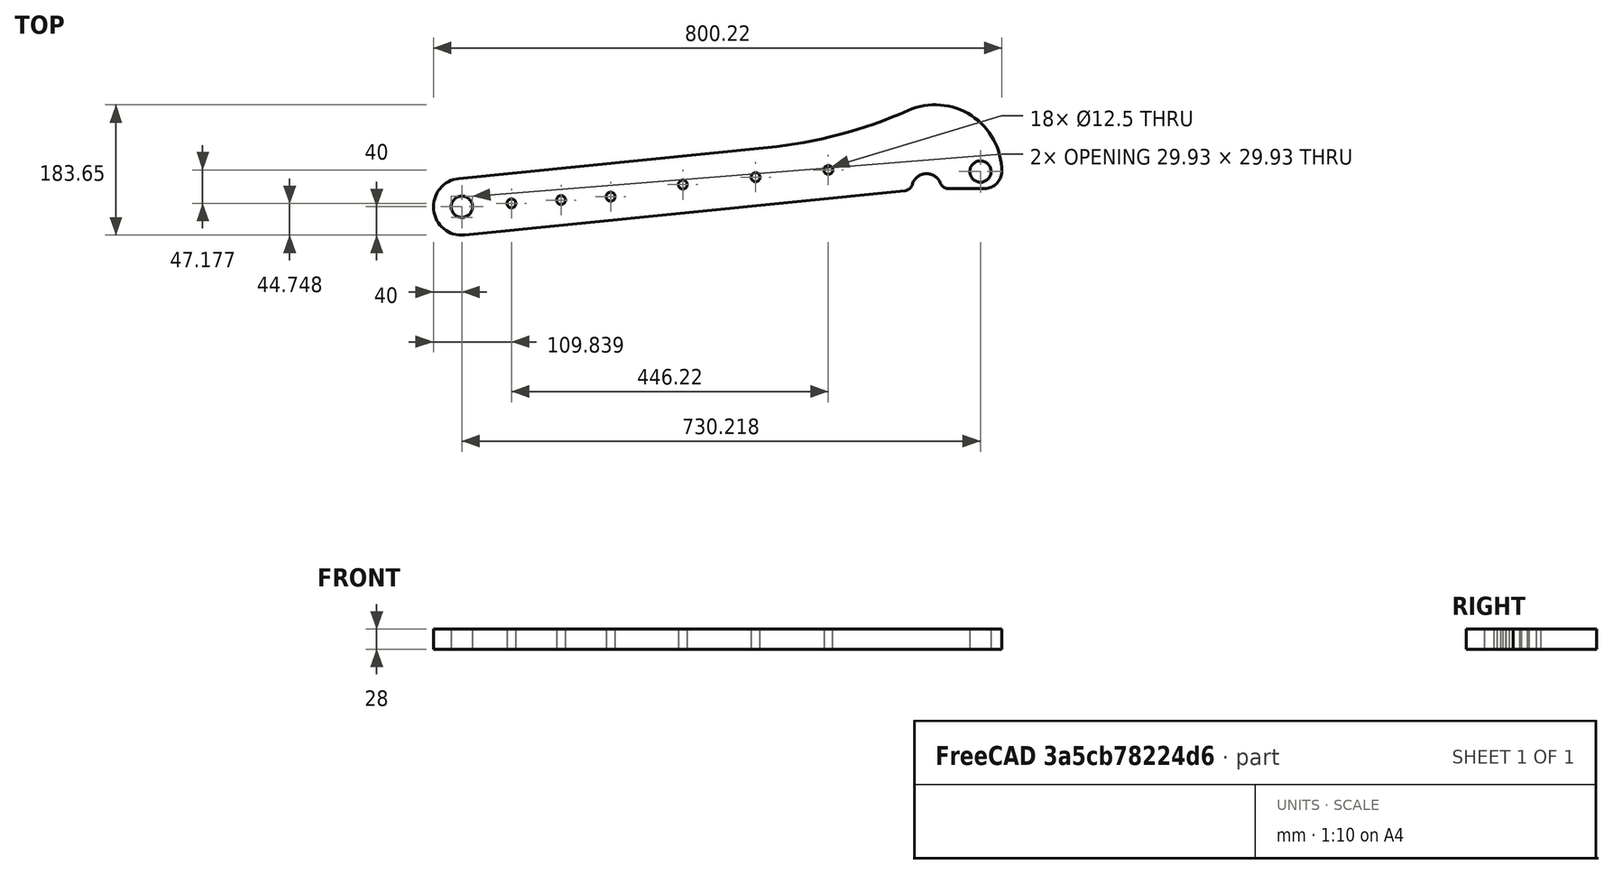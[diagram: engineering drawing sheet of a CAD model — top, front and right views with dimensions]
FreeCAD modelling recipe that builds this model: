
FCSTD DOCUMENT  (FreeCAD 0.19R24267 +99 (Git))
Label: V2 Stack pivot arm FEA_CLEARED
License: All rights reserved
LicenseURL: http://en.wikipedia.org/wiki/All_rights_reserved
objects: PartDesign::Pad×3, Fem::ConstraintForce×2, Sketcher::SketchObject×1, Fem::FemSolverObjectPython×1, App::MaterialObjectPython×1, Fem::FeaturePython×1, Fem::FemMeshObjectPython×1, Fem::ConstraintFixed×1, Fem::FemAnalysis×1, PartDesign::Body×1
note: 8 computed .brp shape members not serialized (recipe doc carries the construction recipe); baked Part::Feature solids carry a one-line shape summary decoded from their .brp

FEATURE [Sketcher::SketchObject] Sketch
  FullyConstrained = true
  MapMode = 5
  Support = -> [XY_Plane]
  sketch-geometry (36):
    g0: LineSegment StartX=730.218 StartY=49.6455 StartZ=0 EndX=730.218 EndY=0 EndZ=0
    g1: LineSegment StartX=730.218 StartY=25.6455 StartZ=0 EndX=685.168 EndY=25.6455 EndZ=0
    g2: Circle CenterX=730.218 CenterY=0 CenterZ=0 NormalX=0 NormalY=0 NormalZ=1 AngleXU=0 Radius=15
    g3: ArcOfCircle CenterX=0 CenterY=0 CenterZ=0 NormalX=0 NormalY=0 NormalZ=1 AngleXU=0 Radius=40 StartAngle=1.67108 EndAngle=4.81267
    g4: LineSegment StartX=4.00452 StartY=-39.799 StartZ=0 EndX=623.841 EndY=22.5679 EndZ=0
    g5: LineSegment StartX=730.218 StartY=25.6455 StartZ=0 EndX=736.218 EndY=25.6455 EndZ=0
    g6: ArcOfCircle CenterX=736.218 CenterY=49.6455 CenterZ=0 NormalX=0 NormalY=0 NormalZ=1 AngleXU=0 Radius=24 StartAngle=4.71239 EndAngle=6.28319
    g7: LineSegment StartX=430.857 StartY=83.5541 StartZ=0 EndX=-4.00452 EndY=39.799 EndZ=0
    g8: LineSegment StartX=0 StartY=0 StartZ=0 EndX=730.218 EndY=49.6455 EndZ=0
    g9: LineSegment StartX=0 StartY=0 StartZ=0 EndX=516.059 EndY=51.9251 EndZ=0
    g10: Circle CenterX=311.094 CenterY=31.3018 CenterZ=0 NormalX=0 NormalY=0 NormalZ=1 AngleXU=0 Radius=6.25
    g11: Circle CenterX=413.577 CenterY=41.6134 CenterZ=0 NormalX=0 NormalY=0 NormalZ=1 AngleXU=0 Radius=6.25
    g12: GeomPoint X=730.218 Y=24 Z=0
    g13: LineSegment StartX=0 StartY=0 StartZ=0 EndX=-1.01746 EndY=14.9655 EndZ=0
    g14: LineSegment StartX=0 StartY=0 StartZ=0 EndX=1.01746 EndY=-14.9655 EndZ=0
    g15: ArcOfCircle CenterX=0 CenterY=0 CenterZ=0 NormalX=0 NormalY=0 NormalZ=1 AngleXU=0 Radius=15 StartAngle=1.63868 EndAngle=4.78027
    g16: ArcOfCircle CenterX=0 CenterY=0 CenterZ=0 NormalX=0 NormalY=0 NormalZ=1 AngleXU=0 Radius=15 StartAngle=4.78027 EndAngle=7.92186
    g17: LineSegment StartX=730.218 StartY=49.6455 StartZ=0 EndX=729.201 EndY=64.611 EndZ=0
    g18: LineSegment StartX=730.218 StartY=49.6455 StartZ=0 EndX=731.236 EndY=34.68 EndZ=0
    g19: ArcOfCircle CenterX=730.218 CenterY=49.6455 CenterZ=0 NormalX=0 NormalY=0 NormalZ=1 AngleXU=0 Radius=15 StartAngle=4.78027 EndAngle=7.92186
    g20: ArcOfCircle CenterX=730.218 CenterY=49.6455 CenterZ=0 NormalX=0 NormalY=0 NormalZ=1 AngleXU=0 Radius=15 StartAngle=1.63868 EndAngle=4.78027
    g21: Circle CenterX=516.059 CenterY=51.9251 CenterZ=0 NormalX=0 NormalY=0 NormalZ=1 AngleXU=0 Radius=6.25
    g22: LineSegment StartX=730.218 StartY=49.6455 StartZ=0 EndX=666.218 EndY=49.6455 EndZ=0
    g23: ArcOfCircle CenterX=666.218 CenterY=49.6455 CenterZ=0 NormalX=0 NormalY=0 NormalZ=1 AngleXU=0 Radius=94 StartAngle=0 EndAngle=1.98647
    g24: ArcOfCircle CenterX=365.784 CenterY=730.289 CenterZ=0 NormalX=0 NormalY=0 NormalZ=1 AngleXU=0 Radius=650 StartAngle=4.81267 EndAngle=5.12807
    g25: Circle CenterX=516.059 CenterY=51.9251 CenterZ=0 NormalX=0 NormalY=0 NormalZ=1 AngleXU=0 Radius=40
    g26: Circle CenterX=209.516 CenterY=14.2444 CenterZ=0 NormalX=0 NormalY=0 NormalZ=1 AngleXU=0 Radius=6.25
    g27: Circle CenterX=139.678 CenterY=9.49629 CenterZ=0 NormalX=0 NormalY=0 NormalZ=1 AngleXU=0 Radius=6.25
    g28: Circle CenterX=69.8388 CenterY=4.74814 CenterZ=0 NormalX=0 NormalY=0 NormalZ=1 AngleXU=0 Radius=6.25
    g29: ArcOfCircle CenterX=654.427 CenterY=25.6455 CenterZ=0 NormalX=0 NormalY=0 NormalZ=1 AngleXU=0 Radius=21 StartAngle=0.372169 EndAngle=2.86971
    g30: ArcOfCircle CenterX=622.64 CenterY=34.5077 CenterZ=0 NormalX=0 NormalY=0 NormalZ=1 AngleXU=0 Radius=12 StartAngle=4.81267 EndAngle=6.0113
    g31: ArcOfCircle CenterX=685.168 CenterY=37.6455 CenterZ=0 NormalX=0 NormalY=0 NormalZ=1 AngleXU=0 Radius=12 StartAngle=3.51376 EndAngle=4.71239
    g32: LineSegment StartX=654.427 StartY=25.6455 StartZ=0 EndX=685.168 EndY=25.6455 EndZ=0
    g33: LineSegment StartX=623.841 StartY=22.5679 StartZ=0 EndX=654.427 EndY=25.6455 EndZ=0
    g34: Circle CenterX=0 CenterY=0 CenterZ=0 NormalX=0 NormalY=0 NormalZ=1 AngleXU=0 Radius=6.5
    g35: Circle CenterX=730.218 CenterY=49.6455 CenterZ=0 NormalX=0 NormalY=0 NormalZ=1 AngleXU=0 Radius=6.5
  constraints (95):
    c: PointOnObject(g0,g-1)
    c: Vertical(g0)
    c: PointOnObject(g1,g0)
    c: Horizontal(g1)
    c: Coincident(g2,g0)
    c: Coincident(g5,g1)
    c: Horizontal(g5)
    c: Tangent(g5,g6) = -1.5708
    c: Tangent(g3,g7) = -1.5708
    c: Tangent(g3,g4) = -1.5708
    c: Radius(g3) = 40
    c: Radius(g6) = 24
    c: PointOnObject(g10,g9)
    c: PointOnObject(g11,g9)
    c: Distance(g11,g10) = 103
    c: Equal(g10,g11)
    c: PointOnObject(g12,g0)
    c: DistanceY(g2,g12) = 24
    c: Perpendicular(g13,g8)
    c: Perpendicular(g14,g8)
    c: Coincident(g-1,g8)
    c: Coincident(g-1,g9)
    c: Coincident(g3,g-1)
    c: Coincident(g13,g3)
    c: Coincident(g3,g14)
    c: Coincident(g15,g3)
    c: Coincident(g15,g13)
    c: Coincident(g15,g14)
    c: Coincident(g16,g3)
    c: Coincident(g16,g14)
    c: Perpendicular(g17,g8)
    c: Perpendicular(g18,g8)
    c: Coincident(g19,g17)
    c: Coincident(g19,g18)
    c: Coincident(g20,g18)
    c: Coincident(g20,g17)
    c: Distance(g11,g21) = 103
    c: Coincident(g0,g8)
    c: Coincident(g0,g17)
    c: Coincident(g0,g18)
    c: Coincident(g0,g19)
    c: Coincident(g22,g19)
    c: Horizontal(g22)
    c: Coincident(g23,g22)
    c: DistanceX(g0,g6) = 30
    c: DistanceY(g1,g19) = 24
    c: DistanceX(g22,g22) = 64
    c: Tangent(g23,g6) = -1.5708
    c: Distance(g8) = 731.904
    c: DistanceY(g0,g19) = 49.6455
    c: Parallel(g4,g7)
    c: Tangent(g23,g24) = 1.5708
    c: Tangent(g7,g24) = 1.5708
    c: Equal(g2,g19)
    c: Equal(g20,g15)
    c: Coincident(g21,g9)
    c: Coincident(g25,g21)
    c: Tangent(g25,g4)
    c: Tangent(g25,g7)
    c: DistanceY(g12,g1) = 1.6455
    c: Angle(g8,g9) = 0.0323982
    c: Coincident(g0,g20)
    c: Coincident(g16,g15)
    c: Distance(g26,g27) = 70
    c: Distance(g27,g28) = 70
    c: Equal(g28,g27)
    c: Equal(g27,g26)
    c: Equal(g26,g10)
    c: Equal(g21,g28)
    c: Distance(g28,g3) = 70
    c: Radius(g29) = 21
    c: Distance(g29,g19) = 79.5
    c: Radius(g24) = 650
    c: Tangent(g29,g30) = 1.5708
    c: Tangent(g4,g30) = -1.5708
    c: Tangent(g29,g31) = 1.5708
    c: Tangent(g1,g31) = 1.5708
    c: Equal(g30,g31)
    c: Radius(g30) = 12
    c: Coincident(g32,g29)
    c: Coincident(g32,g1)
    c: Horizontal(g32)
    c: Coincident(g33,g4)
    c: Coincident(g33,g29)
    c: Parallel(g33,g4)
    c: PointOnObject(g26,g8)
    c: PointOnObject(g27,g8)
    c: PointOnObject(g28,g8)
    c: Distance(g26,g10) = 103
    c: Diameter(g28) = 12.5
    c: Diameter(g15) = 30
    c: Coincident(g34,g3)
    c: Coincident(g35,g19)
    c: Equal(g35,g34)
    c: Diameter(g34) = 13
FEATURE [PartDesign::Pad] Pad
  Direction = (1,1,1)
  Length = 8
  Length2 = 100
  Profile = -> Sketch
  Type = 0
FEATURE [Fem::FemSolverObjectPython] SolverCcxTools  # FEM object (typed FeaturePython)
  AnalysisType = 0
  BeamShellResultOutput3D = false
  EigenmodeHighLimit = 1000000
  EigenmodeLowLimit = 0
  EigenmodesCount = 10
  GeometricalNonlinearity = 0
  IterationsControlParameterCutb = 0.25,0.5,0.75,0.85,,,1.5,
  IterationsControlParameterIter = 4,8,9,200,10,400,,200,,
  IterationsControlParameterTimeUse = false
  IterationsThermoMechMaximum = 2000
  IterationsUserDefinedIncrementations = false
  IterationsUserDefinedTimeStepLength = false
  MaterialNonlinearity = 0
  MatrixSolverType = 0
  SplitInputWriter = false
  ThermoMechSteadyState = true
  TimeEnd = 1
  TimeInitialStep = 0.01
FEATURE [App::MaterialObjectPython] MaterialSolid  # material (typed FeaturePython)
  Category = 0
  Material = AuthorAndLicense=CalculiX-Steel,CardName=CalculiX-Steel,Density=7900 kg/m^3,Description=Standard steel material for CalculiX sample calculations,+7 more (map truncated)
FEATURE [Fem::FeaturePython] MeshRegion  # FEM object (typed FeaturePython)
  CharacteristicLength = 1.5
  References = -> [Pad]
FEATURE [Fem::FemMeshObjectPython] FEMMeshGmsh  # FEM object (typed FeaturePython)
  Algorithm2D = 0
  Algorithm3D = 0
  CharacteristicLengthMax = 6
  CharacteristicLengthMin = 0
  CoherenceMesh = true
  ElementDimension = 0
  ElementOrder = 1
  GeometryTolerance = 1e-06
  GroupsOfNodes = false
  HighOrderOptimize = false
  MeshRegionList = -> [MeshRegion]
  OptimizeNetgen = false
  OptimizeStd = true
  Part = -> Pad
  RecombineAll = false
  SecondOrderLinear = false
FEATURE [Fem::ConstraintForce] ConstraintForce
  DirectionVector = (0.997697,0.0678306,0)
  Force = 8571
  NormalDirection = (-0.997697,-0.0678306,0)
  Points = (12) [(731.236,34.68,8),(743.688,43.0439,8),(742.67,58.0094,8),(729.201,64.611,8),(731.236,34.68,4),(743.688,43.0439,4),(742.67,58.0094,4),+5 more]
  References = -> [Pad]
  Reversed = true
  Scale = 4
FEATURE [Fem::ConstraintForce] ConstraintForce001
  DirectionVector = (-0.997697,-0.0678306,0)
  Force = 8571
  NormalDirection = (0.997697,0.0678306,0)
  Points = (12) [(-1.01746,14.9655,8),(-13.4692,6.60158,8),(-12.4517,-8.36387,8),(1.01746,-14.9655,8),(-1.01746,14.9655,4),(-13.4692,6.60158,4),(-12.4517,-8.36387,4),+5 more]
  References = -> [Pad]
  Reversed = true
  Scale = 4
FEATURE [Fem::ConstraintFixed] ConstraintFixed
  NormalDirection = (0,0,1)
  Normals = (2) [(0,0,1),(0,0,1)]
  Points = (2) [(4.00452,-39.799,0),(4.00452,-39.799,8)]
  References = -> [Pad]
FEATURE [Fem::FemAnalysis] Analysis  label="Analysis ON ONLY ONE 8mm PLATE"
  Group = -> [SolverCcxTools,MaterialSolid,FEMMeshGmsh,ConstraintForce,ConstraintForce001,ConstraintFixed]
FEATURE [PartDesign::Pad] Pad001
  BaseFeature = -> Pad
  Direction = (1,1,1)
  Length = 12
  Length2 = 100
  Profile = -> Pad [Face23]
  Type = 0
FEATURE [PartDesign::Pad] Pad002
  BaseFeature = -> Pad001
  Direction = (1,1,1)
  Length = 8
  Length2 = 100
  Profile = -> Pad001 [Face26]
  Type = 0
FEATURE [PartDesign::Body] Body
  Group = -> [Sketch,Pad,Pad001,Pad002]
  Origin = -> Origin
  Tip = -> Pad002
